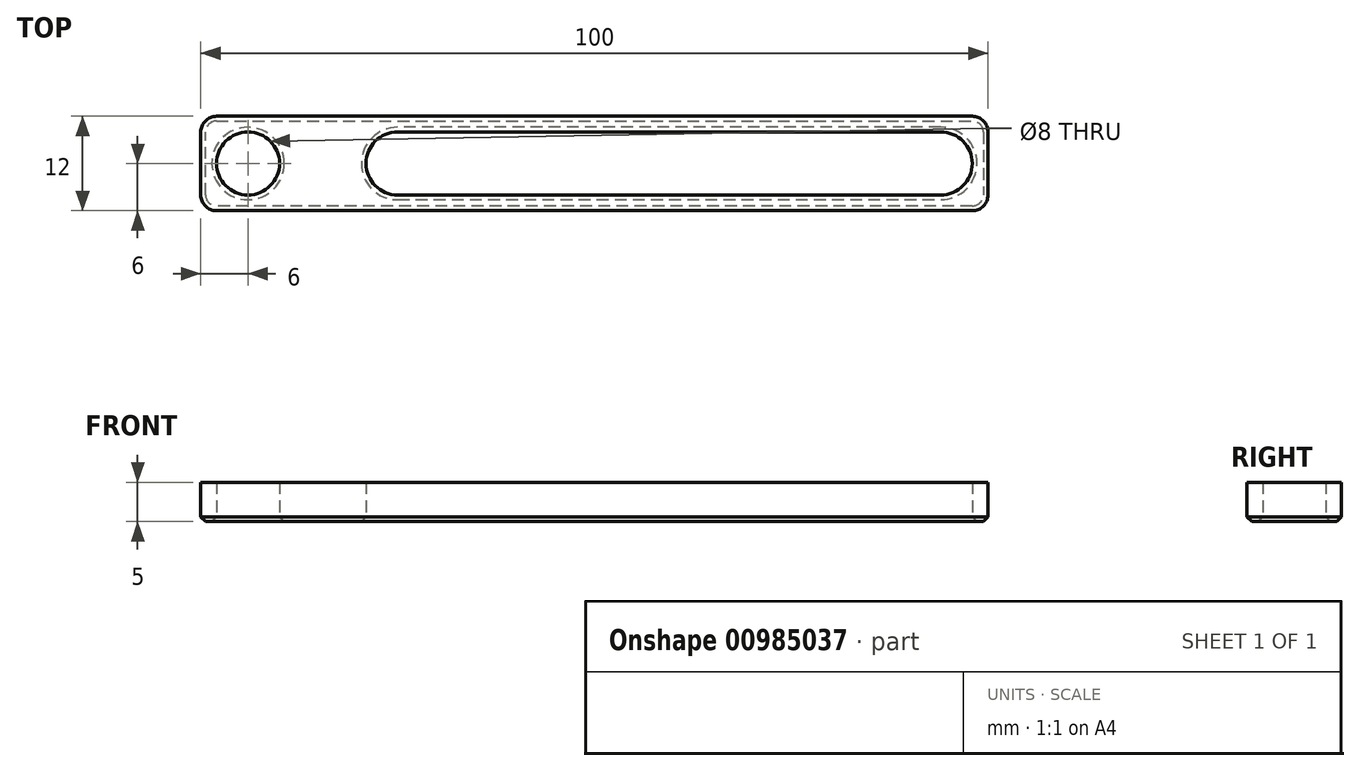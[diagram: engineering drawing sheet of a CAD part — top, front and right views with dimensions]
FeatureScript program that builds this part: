
annotation { "Feature Type Name" : "Feature", "Feature Type Description" : "" }
export const myFeature = defineFeature(function(context is Context, id is Id, definition is map)
    precondition{}
    {
        {
            var Q0;
            Q0=qCreatedBy(makeId("Top.planeOp"),FACE);
            var sketch = newSketch(context, id + "F0", { "sketchPlane" : qUnion([Q0])});
            skLineSegment(sketch, "E0.bottom", {"start": v(-25, 6) * mm, "end": v(75, 6) * mm});
            skLineSegment(sketch, "E0.top", {"start": v(-25, -6) * mm, "end": v(75, -6) * mm});
            skLineSegment(sketch, "E0.left", {"start": v(-25, 6) * mm, "end": v(-25, -6) * mm});
            skLineSegment(sketch, "E0.right", {"start": v(75, 6) * mm, "end": v(75, -6) * mm});
            skCircle(sketch, "E1", {"center": v(-19, 0) * mm, "radius": 4 * mm});
            skLineSegment(sketch, "E2", {"start": v(0, 0) * mm, "end": v(69, 0) * mm, "construction": true});
            skArc(sketch, "E3.0.startCap", {"start": v(0, -4) * mm, "mid": v(-4, 0) * mm, "end": v(0, 4) * mm});
            skArc(sketch, "E3.0.endCap", {"start": v(69, 4) * mm, "mid": v(73, 0) * mm, "end": v(69, -4) * mm});
            skLineSegment(sketch, "E3.0.left", {"start": v(0, 4) * mm, "end": v(69, 4) * mm});
            skLineSegment(sketch, "E3.0.right", {"start": v(0, -4) * mm, "end": v(69, -4) * mm});
            skSolve(sketch);
        }
        {
            var Q0;
            Q0 = qSketchRegion(id + "F0", true);
            extrude(context, id + "F1", {"entities" : qUnion([Q0]), "depth" : 5 * mm, "offsetDistance" : 25 * mm});
        }
        {
            var Q0;
            Q0=makeQuery(id+"F1.opExtrude","SWEPT_EDGE",EDGE,{"disambiguationData":[OSD([sQuery(id+"F0.wireOp",EDGE,"E0.top"),sQuery(id+"F0.wireOp",EDGE,"E0.left")])]});
            var Q1;
            Q1=makeQuery(id+"F1.opExtrude","SWEPT_EDGE",EDGE,{"disambiguationData":[OSD([sQuery(id+"F0.wireOp",EDGE,"E0.bottom"),sQuery(id+"F0.wireOp",EDGE,"E0.left")])]});
            var Q2;
            Q2=makeQuery(id+"F1.opExtrude","SWEPT_EDGE",EDGE,{"disambiguationData":[OSD([sQuery(id+"F0.wireOp",EDGE,"E0.bottom"),sQuery(id+"F0.wireOp",EDGE,"E0.right")])]});
            var Q3;
            Q3=makeQuery(id+"F1.opExtrude","SWEPT_EDGE",EDGE,{"disambiguationData":[OSD([sQuery(id+"F0.wireOp",EDGE,"E0.top"),sQuery(id+"F0.wireOp",EDGE,"E0.right")])]});
            fillet(context, id + "F2", {"entities" : qUnion([Q0, Q1, Q2, Q3]), "tangentPropagation" : true, "radius" : 2 * mm, "defaultsChanged" : true, "vertexSettings" : [], "allowEdgeOverflow" : false});
        }
        {
            var Q0;
            Q0=makeQuery(id+"F1.opExtrude","CAP_FACE",FACE,{"disambiguationData":[OSD([sQuery(id+"F0.wireOp",EDGE,"E0.bottom"),sQuery(id+"F0.wireOp",EDGE,"E0.top"),sQuery(id+"F0.wireOp",EDGE,"E0.left"),sQuery(id+"F0.wireOp",EDGE,"E0.right"),sQuery(id+"F0.wireOp",EDGE,"E1"),sQuery(id+"F0.wireOp",EDGE,"E3.0.startCap"),sQuery(id+"F0.wireOp",EDGE,"E3.0.endCap"),sQuery(id+"F0.wireOp",EDGE,"E3.0.left"),sQuery(id+"F0.wireOp",EDGE,"E3.0.right")])],"isStart":true});
            chamfer(context, id + "F3", {"entities" : qUnion([Q0]), "width" : 0.6 * mm, "tangentPropagation" : true});
        }
    });
